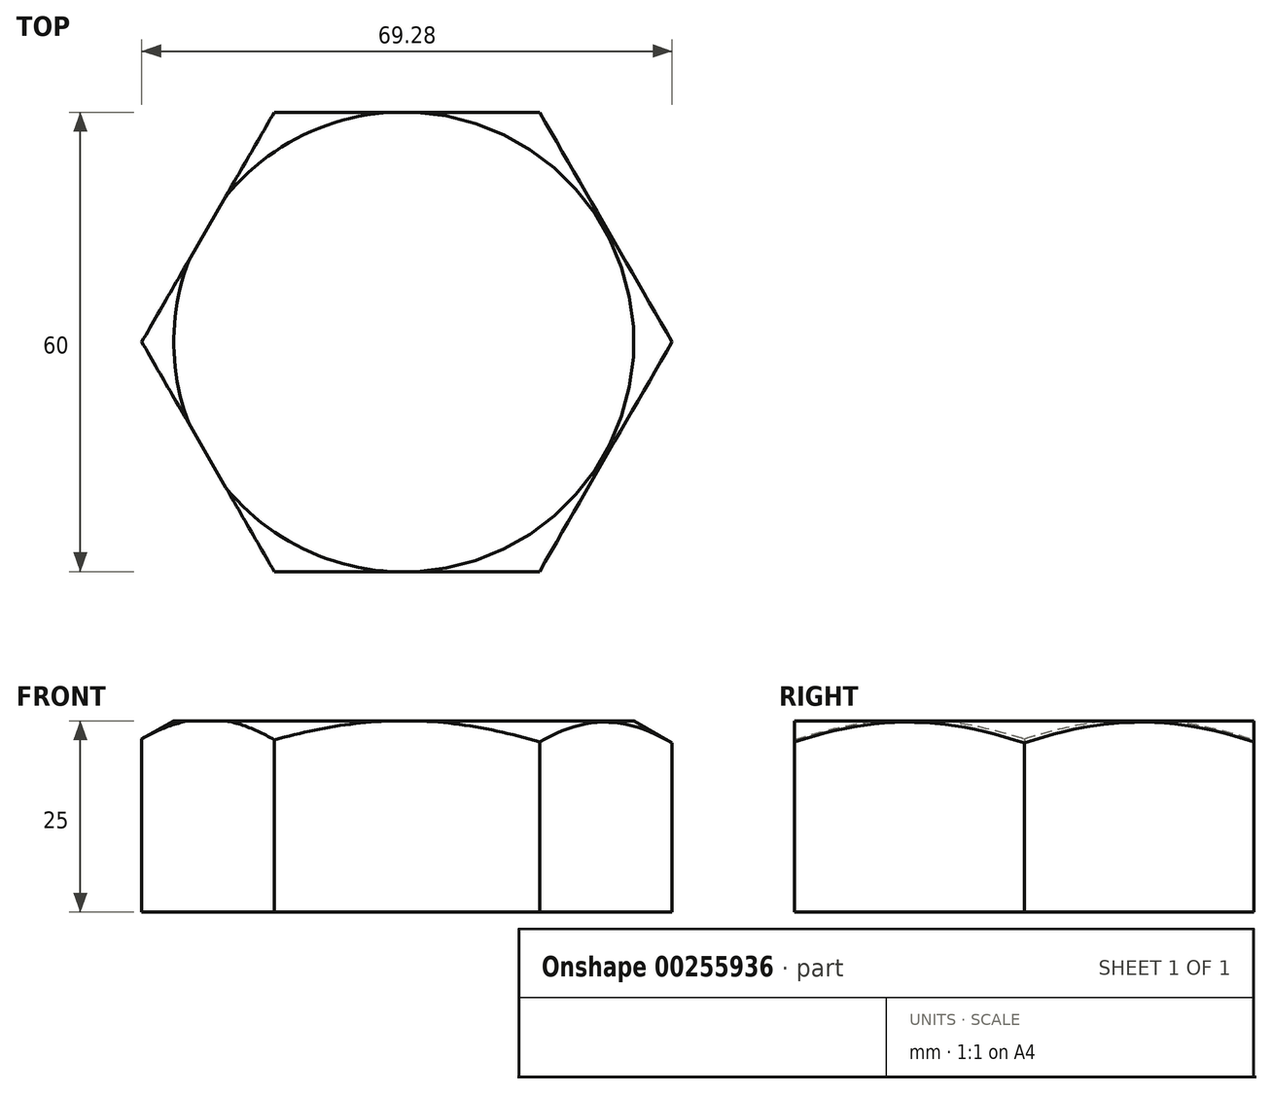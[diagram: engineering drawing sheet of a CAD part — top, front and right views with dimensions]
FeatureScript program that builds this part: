
annotation { "Feature Type Name" : "Feature", "Feature Type Description" : "" }
export const myFeature = defineFeature(function(context is Context, id is Id, definition is map)
    precondition{}
    {
        {
            var Q0;
            Q0=qCreatedBy(makeId("Top.planeOp"),FACE);
            var sketch = newSketch(context, id + "F0", { "sketchPlane" : qUnion([Q0])});
            skCircle(sketch, "E0.cCircle", {"center": v(0, 0) * mm, "radius": 30 * mm, "construction": true});
            skLineSegment(sketch, "E0.0", {"start": v(-17.32, 30) * mm, "end": v(17.32, 30) * mm});
            skLineSegment(sketch, "E0.1", {"start": v(17.32, 30) * mm, "end": v(34.64, 0) * mm});
            skLineSegment(sketch, "E0.2", {"start": v(34.64, 0) * mm, "end": v(17.32, -30) * mm});
            skLineSegment(sketch, "E0.3", {"start": v(17.32, -30) * mm, "end": v(-17.32, -30) * mm});
            skLineSegment(sketch, "E0.4", {"start": v(-17.32, -30) * mm, "end": v(-34.64, 0) * mm});
            skLineSegment(sketch, "E0.5", {"start": v(-34.64, 0) * mm, "end": v(-17.32, 30) * mm});
            skPoint(sketch, "E0.0.midPoint", {"position": v(0, 30) * mm});
            skSolve(sketch);
        }
        {
            var Q0;
            Q0=makeQuery(id+"F0.imprint","IMPRINT",FACE,{"disambiguationData":[TD([[makeQuery(id+"F0.imprint","IMPRINT",EDGE,{"derivedFrom":sQuery(id+"F0.wireOp",EDGE,"E0.0")}),-1.0]])]});
            extrude(context, id + "F1", {"entities" : qUnion([Q0]), "depth" : 25 * mm});
        }
        {
            var Q0;
            Q0=qCreatedBy(makeId("Front.planeOp"),FACE);
            var sketch = newSketch(context, id + "F2", { "sketchPlane" : qUnion([Q0])});
            skLineSegment(sketch, "E1.0", {"start": v(34.64, 25) * mm, "end": v(17.32, 25) * mm});
            skLineSegment(sketch, "E2.0", {"start": v(34.64, 25) * mm, "end": v(34.64, 0) * mm});
            skLineSegment(sketch, "E3", {"start": v(29.64, 25) * mm, "end": v(34.64, 22.11) * mm});
            skLineSegment(sketch, "E4", {"start": v(-0.23, 0.04) * mm, "end": v(0, 37.35) * mm});
            skSolve(sketch);
        }
        {
            var Q0;
            {var subQ3=sQuery(id+"F2.wireOp",EDGE,"E3");Q0=makeQuery(id+"F2.imprint","IMPRINT",FACE,{"disambiguationData":[TD([[makeQuery(id+"F2.imprint","IMPRINT",EDGE,{"derivedFrom":subQ3}),1.0]])]});}
            var Q1;
            Q1=sQuery(id+"F2.wireOp",EDGE,"E4");
            revolve(context, id + "F3", {"operationType" : NewBodyOperationType.REMOVE, "entities" : qUnion([Q0]), "axis" : qUnion([Q1]), "revolveType" : RevolveType.FULL, "oppositeDirection" : true});
        }
    });
